# Revit family: KDW010063
name_source: partatom
category: Plumbing Fixtures
revit_build: Autodesk Revit 2015 (Build: 20140606_1530(x64)
units: mm (PartAtom-declared; Revit-internal decimal feet)

## types (1)
- KDW010063
    BIMobject category = Bath & Spas
    Brand url = http://www.kaldewei.com
    Color = https://www.kaldewei.co.uk
    ColourOptions = https://www.kaldewei.co.uk
    ConnectingDimensions = EN 232
    Design country = Germany
    DrainSize = 52 mm
    Durability = https://www.kaldewei.de
    Edition number = 1
    Features = https://www.kaldewei.co.uk
    Finish = https://www.kaldewei.co.uk
    HasGrabHandles = https:///n
    IFC Classification = Furnishing Element
    IfcExportAs = BATH
    IfcExportType = IfcSanitaryTerminalType
    IntegralAccessories = https://www.kaldewei.co.uk
    Manufacturer = Kaldewei
    Manufacturer country = Germany
    ManufacturerCountry = GERMANY
    ManufacturerName = KALDEWEI
    ManufacturerURL = https://www.kaldewei.com
    Material = steel enamel
    Material main = Steel
    Material secondary = Enamel
    Model = MEISTERSTÜCKCENTRO DUO OVAL
    NBS Reference Code = 35-06-08
    NBS Reference Description = Baths
    Name = MEISTERSTÜCKCENTRO DUO OVAL
    Nominal height = 750 mm
    Nominal width = 1700 mm
    NominalDepth = 485
    NominalLength = 1700
    ObjectName = MEISTERSTÜCK CENTRO DUO OVAL 750x1700x485
    ObjectNorm = EN 14516EU DECLARATION OF PERFORMANCE(https://www.kaldewei.de
    ObjectPicture = https://www.kaldewei.co.uk
    ObjectURL = https://www.kaldewei.co.uk
    PanelMaterial = steel enamel
    Polantis code = KDW010063
    Product Guid = f9a6e9e0-db07-4a69-84e2-bc43425b43f8
    Product SKU = 1127
    Product certification = https://www.kaldewei.co.uk
    Product data url = https://bimobject.com
    Product url = https://www.kaldewei.co.uk
    ProductInformation = Model No.1127: Free-standing design with sensuous elegance: perfectly formed, classic, seamless. Crafted by masters in superior KALDEWEI steel enamel with a 30-year guarantee.
    QR code = http://bimobject.com
    Revision = 1
    SerialNumber = 1127
    Shape = Oval baths
    Size = 750x1700x485
    SupportFrame = https://www.kaldewei.co.uk
    Sustainability = https://kaldewei-fa.secure.footprint.net
    Technical description = https://www.kaldewei.co.uk
    TechnicalDataURL = https://kaldewei.typo-live.web-factory.de
    Type Comments = MEISTERSTÜCK CENTRO DUO OVAL 1127 750x1700x485
    UNSPSC Code = 30181501
    UNSPSCCode = 30181500
    UNSPSCNames = Sanitary ware
    URL = https://www.kaldewei.co.uk
    Uniclass 1.4 Code = L7211
    Uniclass 1.4 Description = Baths
    Uniclass 2.0 Code = PR-35-06-08
    Uniclass 2.0 Description = Baths
    Uniclass 2015 = Pr_40_20_06_08
    Version = 4
    VolumeToOverflowMaximum = 156
    WarrantyDurationParts = 30
    WarrantyDurationUnit = Year
    WarrantyStartDate = https://www.kaldewei.co.uk
    WaterSupplyOverflowAndWasteHolesOverflow = 52 mm
    WaterSupplyOverflowAndWasteHolesWaste = 52 mm
    WaterSupplyOverflowAndWasteHolesWaterSupply = 40/50 mm
    Weight = 120
    Weight Net (Kg) = 120
    finition = Kaldewei

## geometry (parser evidence)
native form markers: Sweep x2
no freeform markers — native parametric forms only
